# Revit family: RIFLESSO-Table
name_source: partatom
category: Lighting Fixtures
units: mm (PartAtom-declared; Revit-internal decimal feet)

## family parameters
Always vertical = Yes
Cut with Voids When Loaded = No
Light Source = No
OmniClass Number = 23.80.70.00
OmniClass Title = Lighting
Part Type = Normal
Room Calculation Point = No
Round Connector Dimension = Use Diameter
Shared = No
Work Plane-Based = Yes

## types (3) — shared parameters
Country = Europe
Default Elevation = 1219 mm
Description = TABLE LAMP
Designer = Studio Debonademeo
Diametr Bulb = 15 mm  [stored 0.0492126 ft]
Manufacturer = Vistosi
Manufacturer country = Italy
Model = RIFLESSO
Type Comments = Studio Debonademeo
URL = https://vistosi.com
URL Product Page = https://vistosi.it
Width = 32 mm
zero-valued in all types: Depth

## per-type parameters (varying)
| type | Lampshade Type |
| RIFLESSO LT2 | RIFLESSO_Lampshade : RIFLESSO LT2 |
| RIFLESSO LT1 | RIFLESSO_Lampshade : RIFLESSO LT1 |
| RIFLESSO LT3 | RIFLESSO_Lampshade : RIFLESSO LT3 |

note: [stored X ft] marks values corroborated as IEEE doubles in the binary element streams (Revit-internal decimal feet)

## geometry (parser evidence)
native form markers: Sweep x6
no freeform markers — native parametric forms only
